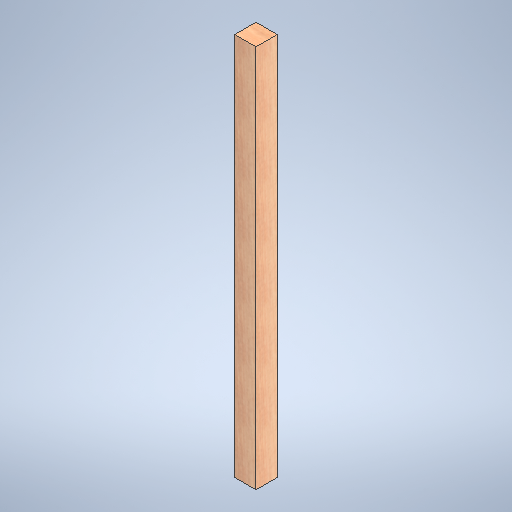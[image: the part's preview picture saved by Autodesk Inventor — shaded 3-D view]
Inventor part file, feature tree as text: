
AUTODESK INVENTOR PART (.ipt)
format: ipt  version: 2025 (Build 290162000, 162)  size: 304,128 bytes
history: native  units: in
note: dims shown in document units (in); Inventor stores cm internally (conversion verified against a paired STEP export)
features: extrude x1, sketch x1
ambient origin geometry x8: Origin, YZ Plane, XZ Plane, XY Plane, X Axis, Y Axis, Z Axis, Center Point
bodies: Solid1 (feature_tree)
feature tree (2):
  extrude  "Extrusion1"  Depth=4.0in
  sketch  "Sketch1"  dims[d0=4.0in d1=4.0in d2=72.0in d3=0.0in d4=0.5in d5=0.0344in d6=0.5in d7=0.0344in]
